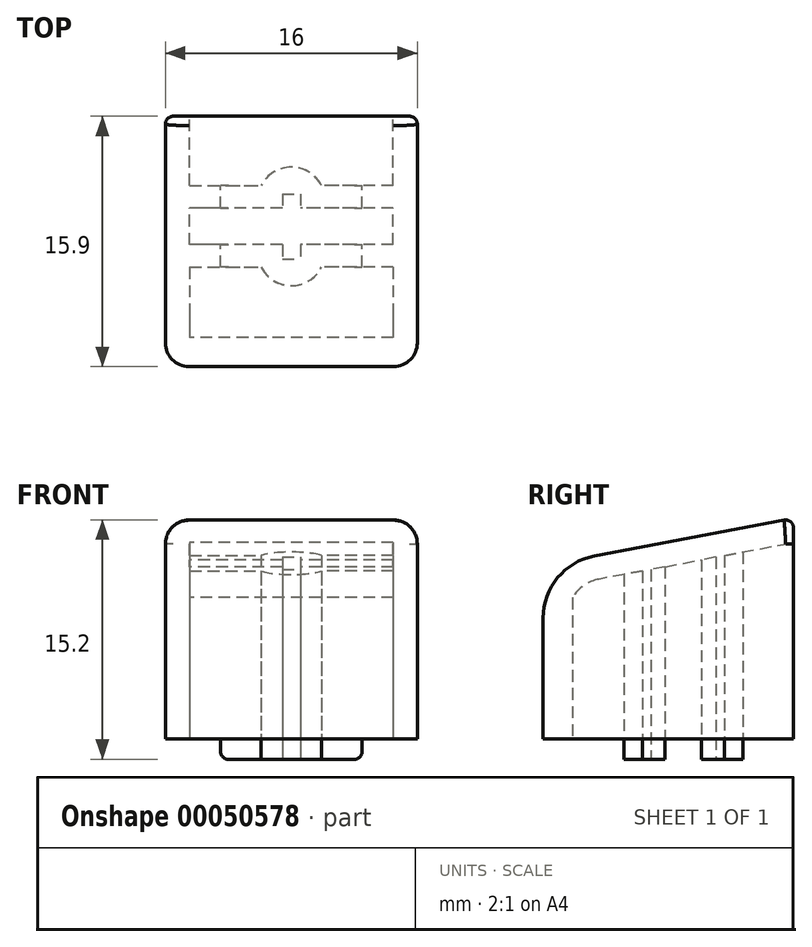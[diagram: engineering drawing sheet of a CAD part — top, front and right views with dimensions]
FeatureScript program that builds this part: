
annotation { "Feature Type Name" : "Feature", "Feature Type Description" : "" }
export const myFeature = defineFeature(function(context is Context, id is Id, definition is map)
    precondition{}
    {
        {
            var Q0;
            Q0=qCreatedBy(makeId("Top.planeOp"),FACE);
            var sketch = newSketch(context, id + "F0", { "sketchPlane" : qUnion([Q0])});
            skLineSegment(sketch, "E0.rect.bottom", {"start": v(6.47, -1.16) * mm, "end": v(-6.47, -1.16) * mm});
            skLineSegment(sketch, "E0.rect.top", {"start": v(6.47, 1.16) * mm, "end": v(-6.47, 1.16) * mm});
            skLineSegment(sketch, "E0.rect.left", {"start": v(6.47, -1.16) * mm, "end": v(6.47, 1.16) * mm});
            skLineSegment(sketch, "E0.rect.right", {"start": v(-6.47, -1.16) * mm, "end": v(-6.47, 1.16) * mm});
            skPoint(sketch, "E0.rect.middle", {"position": v(0, 0) * mm});
            skLineSegment(sketch, "E1.bottom", {"start": v(-8, 7) * mm, "end": v(8, 7) * mm});
            skLineSegment(sketch, "E1.top", {"start": v(-8, -8.9) * mm, "end": v(8, -8.9) * mm});
            skLineSegment(sketch, "E1.left", {"start": v(-8, 7) * mm, "end": v(-8, -8.9) * mm});
            skLineSegment(sketch, "E1.right", {"start": v(8, 7) * mm, "end": v(8, -8.9) * mm});
            skPoint(sketch, "E2", {"position": v(0, -8.9) * mm});
            skLineSegment(sketch, "E3", {"start": v(-6.47, -2.6) * mm, "end": v(-6.47, -7.04) * mm});
            skLineSegment(sketch, "E4", {"start": v(-6.47, -7.04) * mm, "end": v(0, -7.04) * mm});
            skLineSegment(sketch, "E5", {"start": v(0, -7.04) * mm, "end": v(0, -3.77) * mm});
            skLineSegment(sketch, "E6", {"start": v(-6.47, -2.6) * mm, "end": v(-1.91, -2.6) * mm});
            skArc(sketch, "E7", {"start": v(-1.91, -2.6) * mm, "mid": v(0, -3.77) * mm, "end": v(1.91, -2.6) * mm});
            skLineSegment(sketch, "E8.rect.bottom", {"start": v(-0.57, 2.07) * mm, "end": v(0.57, 2.07) * mm});
            skLineSegment(sketch, "E8.rect.top", {"start": v(-0.57, -2.07) * mm, "end": v(0.57, -2.07) * mm});
            skLineSegment(sketch, "E8.rect.left", {"start": v(-0.57, 2.07) * mm, "end": v(-0.57, -2.07) * mm});
            skLineSegment(sketch, "E8.rect.right", {"start": v(0.57, 2.07) * mm, "end": v(0.57, -2.07) * mm});
            skLineSegment(sketch, "E9.MirrorCS", {"start": v(6.47, -2.6) * mm, "end": v(1.91, -2.6) * mm});
            skLineSegment(sketch, "E10.MirrorCS", {"start": v(6.47, -2.6) * mm, "end": v(6.47, -7.04) * mm});
            skLineSegment(sketch, "E11.MirrorCS", {"start": v(6.47, -7.04) * mm, "end": v(0, -7.04) * mm});
            skLineSegment(sketch, "E12", {"start": v(-5.32, 0) * mm, "end": v(5.21, 0) * mm, "construction": true});
            skLineSegment(sketch, "E13.MirrorCS", {"start": v(-6.47, 2.6) * mm, "end": v(-1.91, 2.6) * mm});
            skArc(sketch, "E14.MirrorCS", {"start": v(-1.91, 2.6) * mm, "mid": v(0, 3.77) * mm, "end": v(1.91, 2.6) * mm});
            skLineSegment(sketch, "E15.MirrorCS", {"start": v(6.47, 2.6) * mm, "end": v(1.91, 2.6) * mm});
            skLineSegment(sketch, "E16", {"start": v(-6.47, 2.6) * mm, "end": v(-6.47, 7) * mm});
            skLineSegment(sketch, "E17", {"start": v(6.47, 2.6) * mm, "end": v(6.47, 7) * mm});
            skLineSegment(sketch, "E18", {"start": v(-4.5, -2.6) * mm, "end": v(-4.5, 2.6) * mm});
            skLineSegment(sketch, "E19.MirrorCS", {"start": v(4.5, -2.6) * mm, "end": v(4.5, 2.6) * mm});
            skSolve(sketch);
        }
        {
            var Q0;
            {var subQ15=sQuery(id+"F0.wireOp",EDGE,"E0.rect.left");Q0=makeQuery(id+"F0.imprint","IMPRINT",FACE,{"disambiguationData":[TD([[makeQuery(id+"F0.imprint","IMPRINT",EDGE,{"derivedFrom":subQ15}),-1.0]])]});}
            var Q1;
            {var subQ1=sQuery(id+"F0.wireOp",EDGE,"E8.rect.bottom");Q1=makeQuery(id+"F0.imprint","IMPRINT",FACE,{"disambiguationData":[TD([[makeQuery(id+"F0.imprint","IMPRINT",EDGE,{"derivedFrom":subQ1}),1.0]])]});}
            var Q2;
            {var subQ5=sQuery(id+"F0.wireOp",EDGE,"E8.rect.top");Q2=makeQuery(id+"F0.imprint","IMPRINT",FACE,{"disambiguationData":[TD([[makeQuery(id+"F0.imprint","IMPRINT",EDGE,{"derivedFrom":subQ5}),-1.0]])]});}
            extrude(context, id + "F1", {"entities" : qUnion([Q0, Q1, Q2]), "depth" : 14 * mm});
        }
        {
            var Q0;
            Q0=makeQuery(id+"F1.opExtrude","SWEPT_FACE",FACE,{"disambiguationData":[OSD([sQuery(id+"F0.wireOp",EDGE,"E1.left")])]});
            var sketch = newSketch(context, id + "F2", { "sketchPlane" : qUnion([Q0])});
            skLineSegment(sketch, "E20", {"start": v(-7, 14) * mm, "end": v(8.9, 11) * mm});
            skLineSegment(sketch, "E21.0", {"start": v(8.9, 7.68) * mm, "end": v(8.9, 0) * mm});
            skPoint(sketch, "E22.newPointA", {"position": v(8.9, 14) * mm});
            skArc(sketch, "E22.filletArc", {"start": v(8.9, 7.68) * mm, "mid": v(7.98, 10.24) * mm, "end": v(5.65, 11.61) * mm});
            skArc(sketch, "E23.0", {"start": v(7.4, 7.68) * mm, "mid": v(6.83, 9.28) * mm, "end": v(5.37, 10.14) * mm});
            skLineSegment(sketch, "E23.1", {"start": v(7.4, 7.68) * mm, "end": v(7.4, 0) * mm});
            skLineSegment(sketch, "E24", {"start": v(5.37, 10.14) * mm, "end": v(-7, 12.47) * mm});
            skSolve(sketch);
        }
        {
            var Q0;
            Q0=makeQuery(id+"F2.imprint","IMPRINT",FACE,{"disambiguationData":[TD([[makeQuery(id+"F2.imprint","IMPRINT",EDGE,{"derivedFrom":sQuery(id+"F2.wireOp",EDGE,"E23.0")}),1.0]])]});
            var Q1;
            Q1=makeQuery(id+"F1.opExtrude","SWEPT_FACE",FACE,{"disambiguationData":[OSD([sQuery(id+"F0.wireOp",EDGE,"E1.right")])]});
            extrude(context, id + "F3", {"entities" : qUnion([Q0]), "operationType" : NewBodyOperationType.INTERSECT, "endBound" : BoundingType.UP_TO_SURFACE, "oppositeDirection" : true, "endBoundEntityFace" : qUnion([Q1]), "depth" : 25 * mm});
        }
        {
            var Q0;
            {var subQ1=sQuery(id+"F2.wireOp",EDGE,"E21.0");Q0=makeQuery(id+"F2.imprint","IMPRINT",FACE,{"disambiguationData":[TD([[makeQuery(id+"F2.imprint","IMPRINT",EDGE,{"derivedFrom":subQ1}),-1.0]])]});}
            var Q1;
            Q1=makeQuery(id+"F1.opExtrude","SWEPT_FACE",FACE,{"disambiguationData":[OSD([sQuery(id+"F0.wireOp",EDGE,"E1.right")])]});
            extrude(context, id + "F4", {"entities" : qUnion([Q0]), "operationType" : NewBodyOperationType.ADD, "endBound" : BoundingType.UP_TO_SURFACE, "oppositeDirection" : true, "endBoundEntityFace" : qUnion([Q1]), "depth" : 25 * mm});
        }
        {
            var Q0;
            Q0=makeQuery(id+"F4.opExtrude","CAP_EDGE",EDGE,{"disambiguationData":[OSD([sQuery(id+"F2.wireOp",EDGE,"E20")])],"isStart":true});
            var Q1;
            Q1=makeQuery(id+"F4.opExtrude","CAP_EDGE",EDGE,{"disambiguationData":[OSD([sQuery(id+"F2.wireOp",EDGE,"E20")])],"isStart":false});
            fillet(context, id + "F5", {"entities" : qUnion([Q0, Q1]), "radius" : 1.5 * mm, "tangentPropagation" : true, "allowEdgeOverflow" : false});
        }
        {
            var Q0;
            {var subQ5=sQuery(id+"F0.wireOp",EDGE,"E8.rect.top");Q0=makeQuery(id+"F0.imprint","IMPRINT",FACE,{"disambiguationData":[TD([[makeQuery(id+"F0.imprint","IMPRINT",EDGE,{"derivedFrom":subQ5}),-1.0]])]});}
            var Q1;
            {var subQ1=sQuery(id+"F0.wireOp",EDGE,"E8.rect.bottom");Q1=makeQuery(id+"F0.imprint","IMPRINT",FACE,{"disambiguationData":[TD([[makeQuery(id+"F0.imprint","IMPRINT",EDGE,{"derivedFrom":subQ1}),1.0]])]});}
            extrude(context, id + "F6", {"entities" : qUnion([Q0, Q1]), "operationType" : NewBodyOperationType.ADD, "oppositeDirection" : true, "depth" : 1.3 * mm});
        }
        {
            var Q0;
            {var subQ0=sQuery(id+"F0.wireOp",EDGE,"E18");Q0=makeQuery(id+"F6.opExtrude","CAP_EDGE",EDGE,{"disambiguationData":[OSD([subQ0]),TDD([makeQuery(id+"F0.imprint","IMPRINT",EDGE,{"disambiguationData":[TD([[makeQuery(id+"F0.imprint","INTERSECT",VERTEX,{"derivedFrom":[sQuery(id+"F0.wireOp",EDGE,"E6"),subQ0]}),-1.0]])],"derivedFrom":subQ0})])],"isStart":false});}
            var Q1;
            {var subQ0=sQuery(id+"F0.wireOp",EDGE,"E18");Q1=makeQuery(id+"F6.opExtrude","CAP_EDGE",EDGE,{"disambiguationData":[OSD([subQ0]),TDD([makeQuery(id+"F0.imprint","IMPRINT",EDGE,{"disambiguationData":[TD([[makeQuery(id+"F0.imprint","INTERSECT",VERTEX,{"derivedFrom":[sQuery(id+"F0.wireOp",EDGE,"E13.MirrorCS"),subQ0]}),1.0]])],"derivedFrom":subQ0})])],"isStart":false});}
            var Q2;
            {var subQ0=sQuery(id+"F0.wireOp",EDGE,"E19.MirrorCS");Q2=makeQuery(id+"F6.opExtrude","CAP_EDGE",EDGE,{"disambiguationData":[OSD([subQ0]),TDD([makeQuery(id+"F0.imprint","IMPRINT",EDGE,{"disambiguationData":[TD([[makeQuery(id+"F0.imprint","INTERSECT",VERTEX,{"derivedFrom":[sQuery(id+"F0.wireOp",EDGE,"E9.MirrorCS"),subQ0]}),-1.0]])],"derivedFrom":subQ0})])],"isStart":false});}
            var Q3;
            {var subQ0=sQuery(id+"F0.wireOp",EDGE,"E19.MirrorCS");Q3=makeQuery(id+"F6.opExtrude","CAP_EDGE",EDGE,{"disambiguationData":[OSD([subQ0]),TDD([makeQuery(id+"F0.imprint","IMPRINT",EDGE,{"disambiguationData":[TD([[makeQuery(id+"F0.imprint","INTERSECT",VERTEX,{"derivedFrom":[sQuery(id+"F0.wireOp",EDGE,"E15.MirrorCS"),subQ0]}),1.0]])],"derivedFrom":subQ0})])],"isStart":false});}
            var Q4;
            Q4=makeQuery(id+"F4.opExtrude","SWEPT_EDGE",EDGE,{"disambiguationData":[OSD([sQuery(id+"F0.wireOp",EDGE,"E1.bottom"),sQuery(id+"F0.wireOp",EDGE,"E1.left"),sQuery(id+"F2.wireOp",EDGE,"E20")])]});
            fillet(context, id + "F7", {"entities" : qUnion([Q0, Q1, Q2, Q3, Q4]), "radius" : 0.5 * mm, "tangentPropagation" : true, "allowEdgeOverflow" : false});
        }
    });
